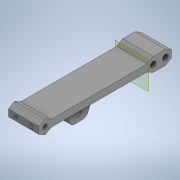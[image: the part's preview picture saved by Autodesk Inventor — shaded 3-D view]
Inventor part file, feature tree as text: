
AUTODESK INVENTOR PART (.ipt)
format: ipt  version: 2020 (Build 240168000, 168)  size: 427,008 bytes
history: native  units: in
note: dims shown in document units (in); Inventor stores cm internally (conversion verified against a paired STEP export)
features: sketch x6, extrude x5, plane x3, projected_geometry x3, mirror x1, fillet x1
ambient origin geometry x8: Origin, YZ Plane, XZ Plane, XY Plane, X Axis, Y Axis, Z Axis, Center Point
bodies: Solid1 (feature_tree)
feature tree (19):
  extrude  "Extrusion1"  Depth=3.4256in
  plane  "Work Plane1"
  sketch  "Sketch4"  dims[d2=0.122in d3=0.7874in]
  extrude  "Extrusion4"  Depth=0.7874in
  plane  "Work Plane2"
  extrude  "Extrusion6"  Depth=3.1106in
  mirror  "Mirror2"
  extrude  "Extrusion8"  Depth=0.315in
  fillet  "Fillet1"  Radius=0.1476in
  sketch  "Sketch11"  dims[d38=0.315in d39=0.2756in d40=-0.3092in d60=1.0994in d61=0.1378in d63=1.1811in d64=0.1575in d65=0.0in d66=0.126in d67=0.1575in d69=0.1949in d70=0.0984in d71=0.3937in d72=0.3937in d73=0.0in]
  plane  "Work Plane3"
  extrude  "Extrusion9"  TaperAngle=0.0deg  [1 undecoded]
  sketch  "Sketch1"  dims[d0=0.1818in d1=3.4256in]
  sketch  "Sketch5"  dims[d4=0.0in d28=3.1106in]
  sketch  "Sketch7"  dims[d29=0.315in d31=0.315in d33=0.1476in]
  projected_geometry  "Projected Loop7"
  projected_geometry  "Projected Loop8"
  sketch  "Sketch10"  dims[d34=0.2362in d35=0.0in]
  projected_geometry  "Projected Loop10"
note: 1 required parameter value undecoded (feature->parameter linkage not recoverable at this tier; creation-order binding heuristic only, values carry confidence <= 0.55)
